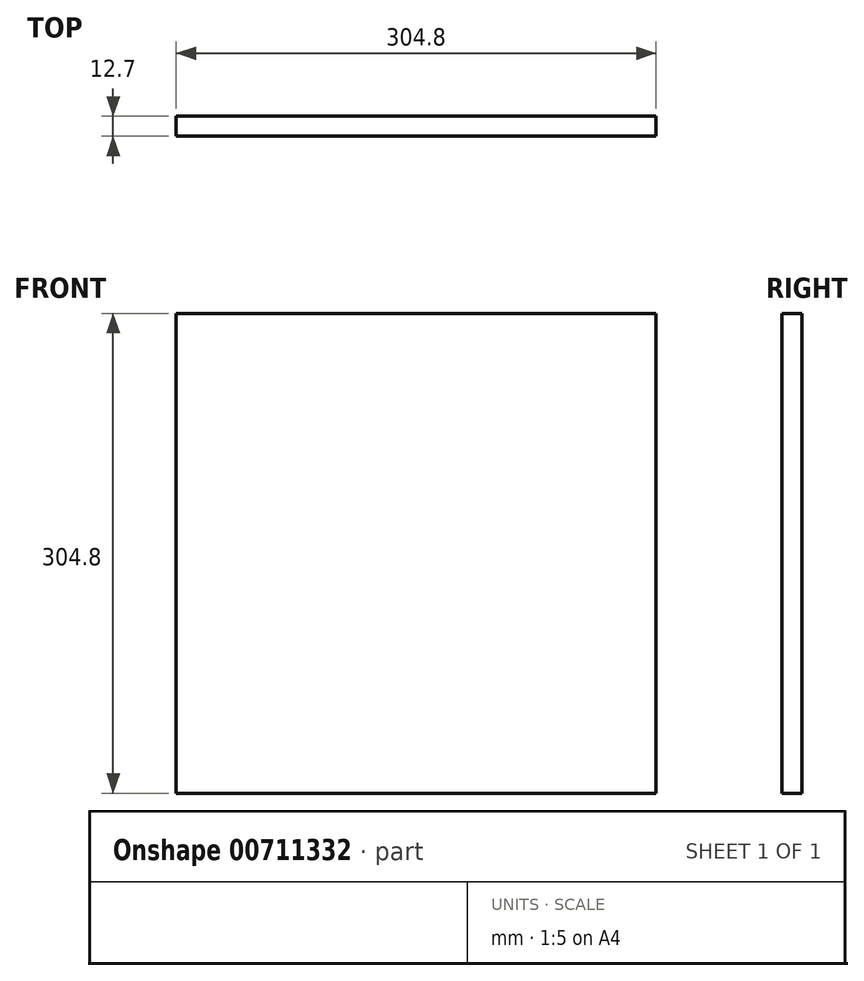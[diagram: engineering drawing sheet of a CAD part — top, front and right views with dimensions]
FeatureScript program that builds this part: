
annotation { "Feature Type Name" : "Feature", "Feature Type Description" : "" }
export const myFeature = defineFeature(function(context is Context, id is Id, definition is map)
    precondition{}
    {
        {
            var Q0;
            Q0=qCreatedBy(makeId("Front.planeOp"),FACE);
            var sketch = newSketch(context, id + "F0", { "sketchPlane" : qUnion([Q0])});
            skLineSegment(sketch, "E0.top", {"start": v(152.4, -152.4) * mm, "end": v(-152.4, -152.4) * mm});
            skLineSegment(sketch, "E0.left", {"start": v(152.4, 152.4) * mm, "end": v(152.4, -152.4) * mm});
            skPoint(sketch, "E0.middle", {"position": v(0, 0) * mm});
            skLineSegment(sketch, "E1", {"start": v(-23.45, 161.54) * mm, "end": v(-23.45, 152.4) * mm});
            skPoint(sketch, "E2.orphan", {"position": v(-152.4, 152.4) * mm});
            skPoint(sketch, "E3.orphan", {"position": v(-23.45, 126.92) * mm});
            skLineSegment(sketch, "E4", {"start": v(152.4, 152.4) * mm, "end": v(-152.4, 152.4) * mm});
            skPoint(sketch, "E5.orphan", {"position": v(-125.03, 35.17) * mm});
            skPoint(sketch, "E6.end.orphan", {"position": v(-137.39, 35.17) * mm});
            skPoint(sketch, "E6.start.orphan", {"position": v(-149.75, 35.17) * mm});
            skLineSegment(sketch, "E7", {"start": v(-152.4, 152.4) * mm, "end": v(-152.4, -152.4) * mm});
            skSolve(sketch);
        }
        {
            var Q0;
            Q0 = qSketchRegion(id + "F0", true);
            extrude(context, id + "F1", {"entities" : qUnion([Q0]), "depth" : 12.7 * mm, "offsetDistance" : 25.4 * mm});
        }
    });
